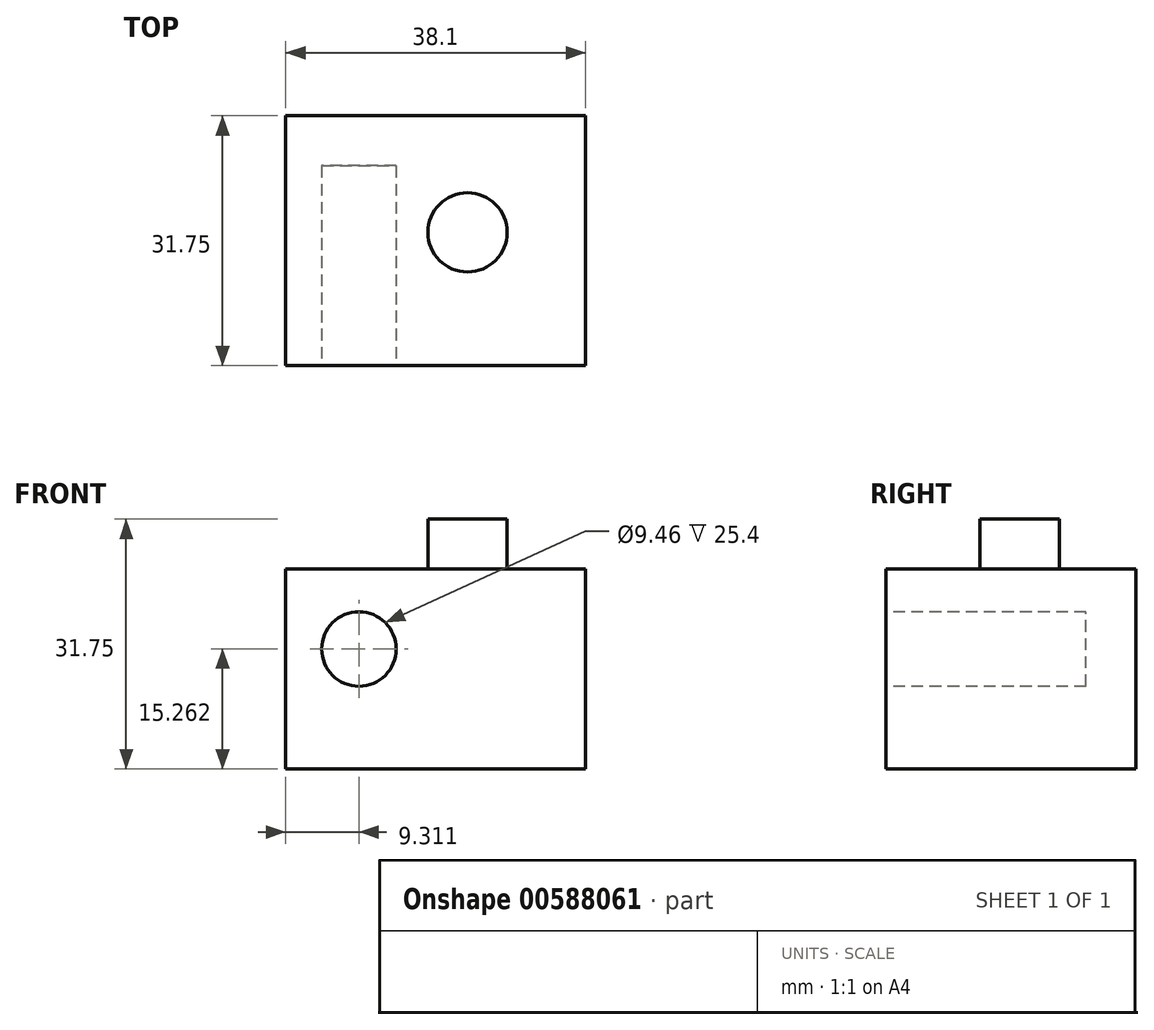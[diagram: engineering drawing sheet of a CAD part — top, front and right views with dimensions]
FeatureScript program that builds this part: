
annotation { "Feature Type Name" : "Feature", "Feature Type Description" : "" }
export const myFeature = defineFeature(function(context is Context, id is Id, definition is map)
    precondition{}
    {
        {
            var Q0;
            Q0=qCreatedBy(makeId("Top.planeOp"),FACE);
            var sketch = newSketch(context, id + "F0", { "sketchPlane" : qUnion([Q0])});
            skLineSegment(sketch, "E0.bottom", {"start": v(0, 0) * mm, "end": v(38.1, 0) * mm});
            skLineSegment(sketch, "E0.top", {"start": v(0, 31.75) * mm, "end": v(38.1, 31.75) * mm});
            skLineSegment(sketch, "E0.left", {"start": v(0, 0) * mm, "end": v(0, 31.75) * mm});
            skLineSegment(sketch, "E0.right", {"start": v(38.1, 0) * mm, "end": v(38.1, 31.75) * mm});
            skSolve(sketch);
        }
        {
            var Q0;
            Q0 = qSketchRegion(id + "F0", true);
            extrude(context, id + "F1", {"entities" : qUnion([Q0]), "depth" : 25.4 * mm, "offsetDistance" : 25.4 * mm});
        }
        {
            var Q0;
            Q0=qCreatedBy(makeId("Front.planeOp"),FACE);
            var sketch = newSketch(context, id + "F2", { "sketchPlane" : qUnion([Q0])});
            skCircle(sketch, "E1", {"center": v(9.31, 15.26) * mm, "radius": 4.73 * mm});
            skSolve(sketch);
        }
        {
            var Q0;
            Q0 = qSketchRegion(id + "F2", true);
            extrude(context, id + "F3", {"entities" : qUnion([Q0]), "operationType" : NewBodyOperationType.REMOVE, "oppositeDirection" : true, "depth" : 25.4 * mm, "offsetDistance" : 25.4 * mm});
        }
        {
            var Q0;
            Q0=makeQuery(id+"F1.opExtrude","CAP_FACE",FACE,{"disambiguationData":[OSD([sQuery(id+"F0.wireOp",EDGE,"E0.bottom"),sQuery(id+"F0.wireOp",EDGE,"E0.top"),sQuery(id+"F0.wireOp",EDGE,"E0.left"),sQuery(id+"F0.wireOp",EDGE,"E0.right")])],"isStart":false});
            var sketch = newSketch(context, id + "F4", { "sketchPlane" : qUnion([Q0])});
            skCircle(sketch, "E2", {"center": v(23.1, 16.94) * mm, "radius": 5.03 * mm});
            skSolve(sketch);
        }
        {
            var Q0;
            Q0 = qSketchRegion(id + "F4", true);
            extrude(context, id + "F5", {"entities" : qUnion([Q0]), "operationType" : NewBodyOperationType.ADD, "depth" : 6.35 * mm, "offsetDistance" : 25.4 * mm});
        }
    });
